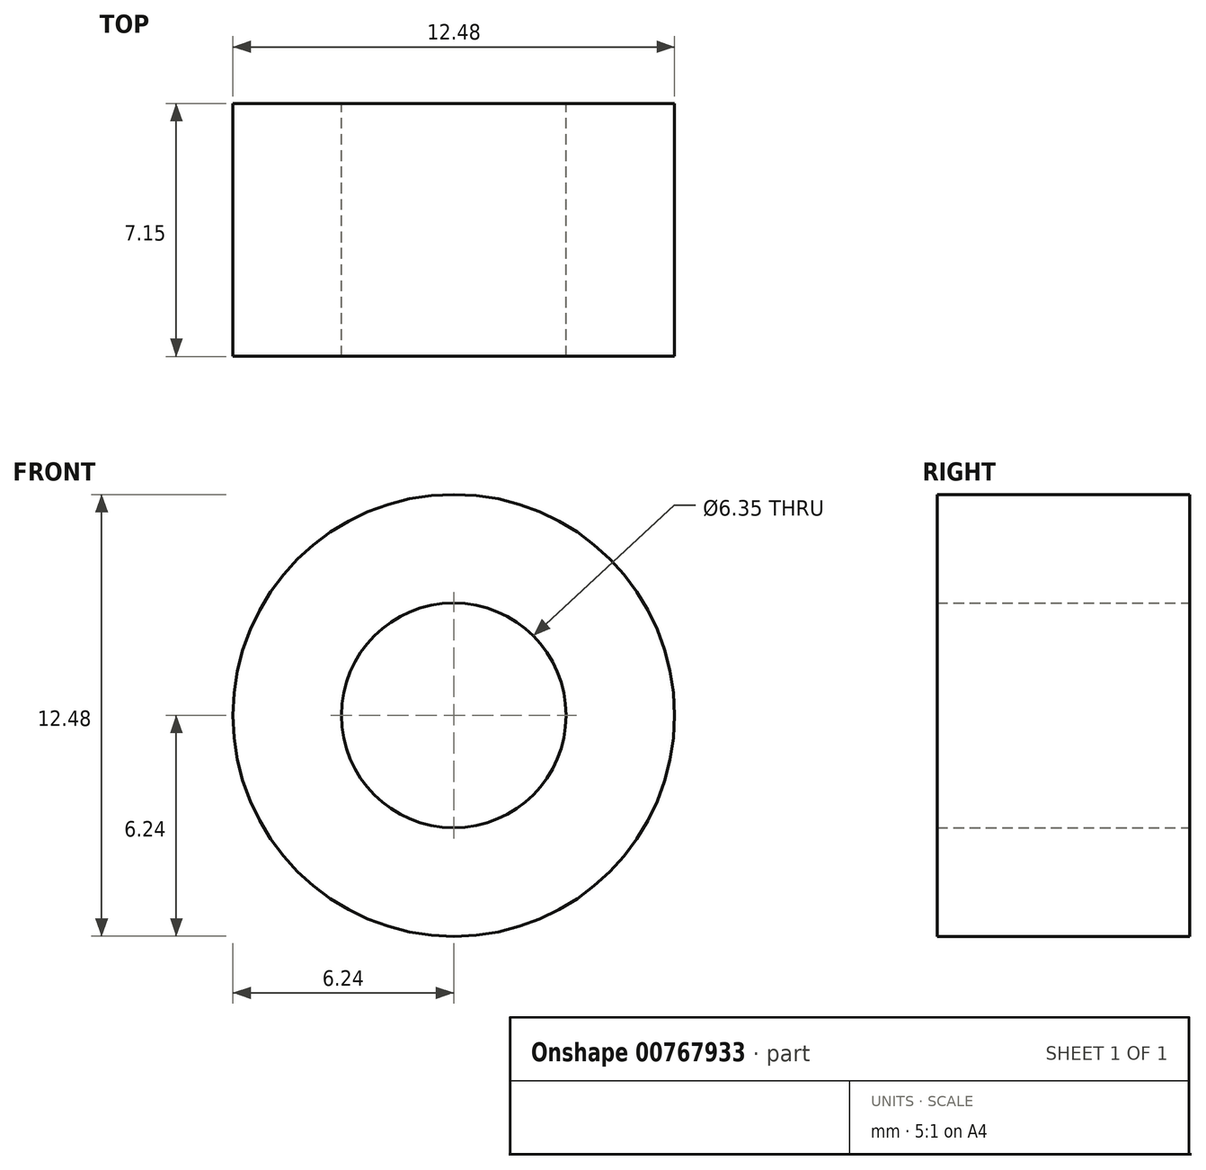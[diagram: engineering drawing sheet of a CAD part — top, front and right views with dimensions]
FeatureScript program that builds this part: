
annotation { "Feature Type Name" : "Feature", "Feature Type Description" : "" }
export const myFeature = defineFeature(function(context is Context, id is Id, definition is map)
    precondition{}
    {
        {
            var Q0;
            Q0=qCreatedBy(makeId("Front.planeOp"),FACE);
            var sketch = newSketch(context, id + "F0", { "sketchPlane" : qUnion([Q0])});
            skCircle(sketch, "E0", {"center": v(0, 0) * mm, "radius": 3.17 * mm});
            skCircle(sketch, "E1", {"center": v(0, 0) * mm, "radius": 6.24 * mm});
            skSolve(sketch);
        }
        {
            var Q0;
            Q0=makeQuery(id+"F0.imprint","IMPRINT",FACE,{"disambiguationData":[TD([[makeQuery(id+"F0.imprint","IMPRINT",EDGE,{"derivedFrom":sQuery(id+"F0.wireOp",EDGE,"E0")}),-1.0]])]});
            extrude(context, id + "F1", {"entities" : qUnion([Q0]), "depth" : (0.28 * 25.4) * mm, "offsetDistance" : 25 * mm});
        }
    });
